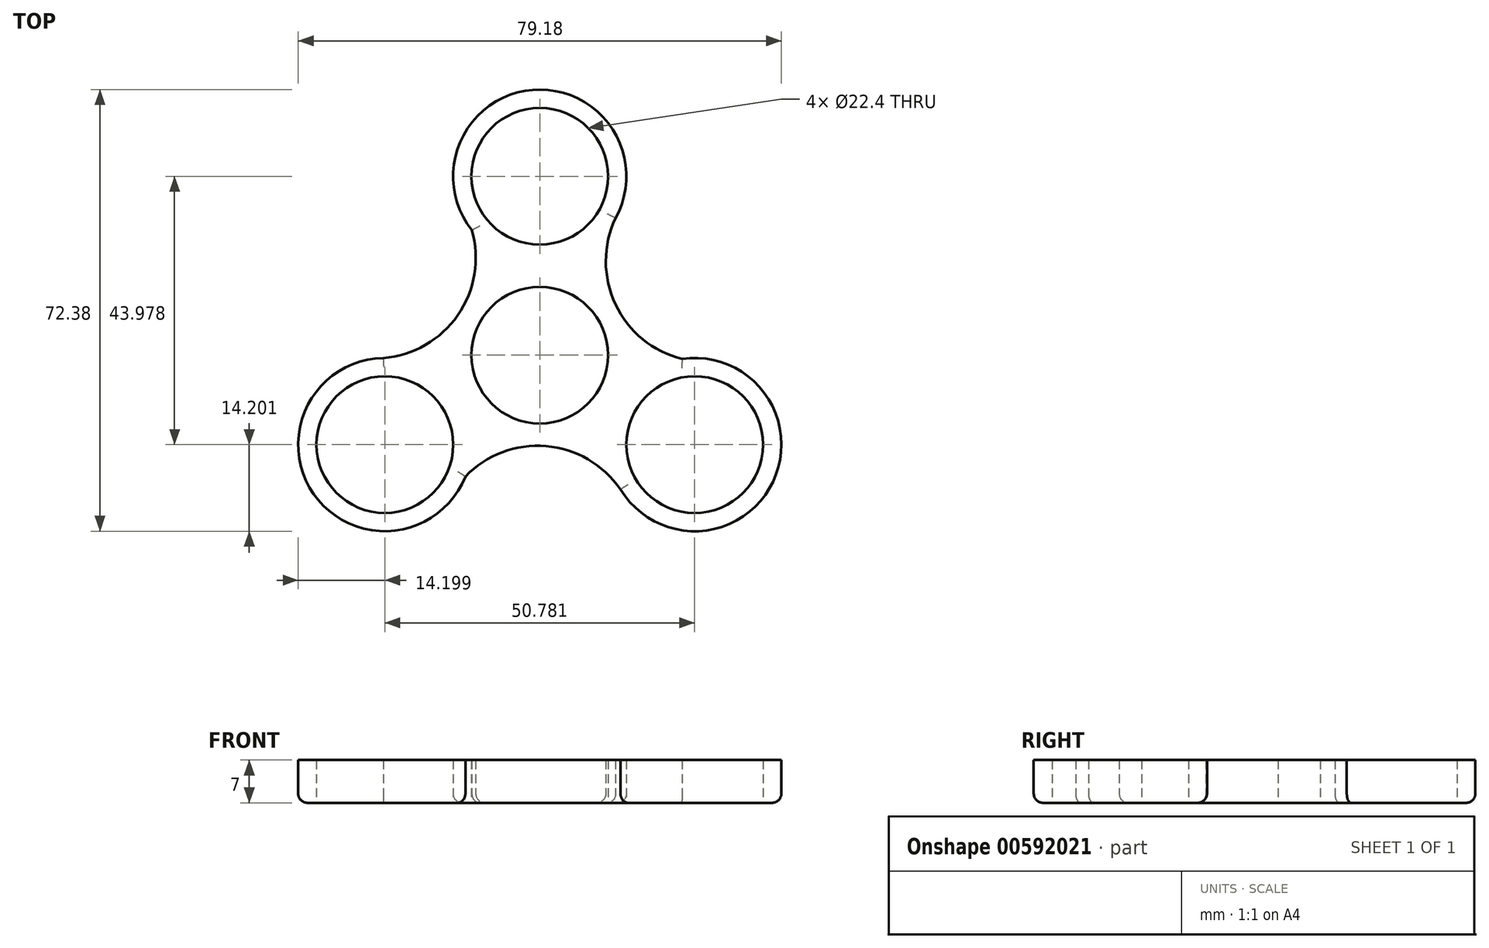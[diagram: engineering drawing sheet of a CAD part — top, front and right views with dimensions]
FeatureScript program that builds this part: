
annotation { "Feature Type Name" : "Feature", "Feature Type Description" : "" }
export const myFeature = defineFeature(function(context is Context, id is Id, definition is map)
    precondition{}
    {
        {
            var Q0;
            Q0=qCreatedBy(makeId("Top.planeOp"),FACE);
            var sketch = newSketch(context, id + "F0", { "sketchPlane" : qUnion([Q0])});
            skCircle(sketch, "E0", {"center": v(0, 0) * mm, "radius": 11.2 * mm});
            skCircle(sketch, "E1", {"center": v(0, 0) * mm, "radius": 14.2 * mm});
            skCircle(sketch, "E2", {"center": v(0, 29.32) * mm, "radius": 11.2 * mm});
            skCircle(sketch, "E3", {"center": v(0, 29.32) * mm, "radius": 14.2 * mm});
            skCircle(sketch, "E4.1.0", {"center": v(-25.4, -14.66) * mm, "radius": 11.2 * mm});
            skCircle(sketch, "E4.1.1", {"center": v(-25.4, -14.66) * mm, "radius": 14.2 * mm});
            skCircle(sketch, "E4.2.0", {"center": v(25.4, -14.66) * mm, "radius": 11.2 * mm});
            skCircle(sketch, "E4.2.1", {"center": v(25.4, -14.66) * mm, "radius": 14.2 * mm});
            skArc(sketch, "E5", {"start": v(12.43, 22.45) * mm, "mid": v(12.4, 8.34) * mm, "end": v(23.32, -0.61) * mm});
            skArc(sketch, "E6.1.0", {"start": v(-25.66, -0.46) * mm, "mid": v(-13.42, 6.57) * mm, "end": v(-11.13, 20.5) * mm});
            skArc(sketch, "E6.2.0", {"start": v(13.23, -21.99) * mm, "mid": v(1.02, -14.9) * mm, "end": v(-12.19, -19.9) * mm});
            skSolve(sketch);
        }
        {
            var Q0;
            Q0=makeQuery(id+"F0.imprint","IMPRINT",FACE,{"disambiguationData":[TD([[makeQuery(id+"F0.imprint","IMPRINT",EDGE,{"derivedFrom":sQuery(id+"F0.wireOp",EDGE,"E1")}),-1.0]])]});
            var Q1;
            Q1=makeQuery(id+"F0.imprint","IMPRINT",FACE,{"disambiguationData":[TD([[makeQuery(id+"F0.imprint","IMPRINT",EDGE,{"derivedFrom":sQuery(id+"F0.wireOp",EDGE,"E4.2.0")}),-1.0]])]});
            var Q2;
            Q2=makeQuery(id+"F0.imprint","IMPRINT",FACE,{"disambiguationData":[TD([[makeQuery(id+"F0.imprint","IMPRINT",EDGE,{"derivedFrom":sQuery(id+"F0.wireOp",EDGE,"E4.1.0")}),-1.0]])]});
            var Q3;
            Q3=makeQuery(id+"F0.imprint","IMPRINT",FACE,{"disambiguationData":[TD([[makeQuery(id+"F0.imprint","IMPRINT",EDGE,{"derivedFrom":sQuery(id+"F0.wireOp",EDGE,"E2")}),-1.0]])]});
            var Q4;
            Q4=makeQuery(id+"F0.imprint","IMPRINT",FACE,{"disambiguationData":[TD([[makeQuery(id+"F0.imprint","IMPRINT",EDGE,{"derivedFrom":sQuery(id+"F0.wireOp",EDGE,"E0")}),-1.0]])]});
            extrude(context, id + "F1", {"entities" : qUnion([Q0, Q1, Q2, Q3, Q4]), "depth" : 7 * mm, "offsetDistance" : 25 * mm});
        }
        {
            var Q0;
            Q0=makeQuery(id+"F1.opExtrude","CAP_EDGE",EDGE,{"disambiguationData":[OSD([sQuery(id+"F0.wireOp",EDGE,"E6.2.0")])],"isStart":true});
            var Q1;
            Q1=makeQuery(id+"F1.opExtrude","CAP_EDGE",EDGE,{"disambiguationData":[OSD([sQuery(id+"F0.wireOp",EDGE,"E4.2.1")])],"isStart":true});
            var Q2;
            Q2=makeQuery(id+"F1.opExtrude","CAP_EDGE",EDGE,{"disambiguationData":[OSD([sQuery(id+"F0.wireOp",EDGE,"E5")])],"isStart":true});
            var Q3;
            Q3=makeQuery(id+"F1.opExtrude","CAP_EDGE",EDGE,{"disambiguationData":[OSD([sQuery(id+"F0.wireOp",EDGE,"E3")])],"isStart":true});
            var Q4;
            Q4=makeQuery(id+"F1.opExtrude","CAP_EDGE",EDGE,{"disambiguationData":[OSD([sQuery(id+"F0.wireOp",EDGE,"E6.1.0")])],"isStart":true});
            var Q5;
            Q5=makeQuery(id+"F1.opExtrude","CAP_EDGE",EDGE,{"disambiguationData":[OSD([sQuery(id+"F0.wireOp",EDGE,"E4.1.1")])],"isStart":true});
            fillet(context, id + "F2", {"entities" : qUnion([Q0, Q1, Q2, Q3, Q4, Q5]), "radius" : 1.5 * mm, "tangentPropagation" : true, "allowEdgeOverflow" : false});
        }
    });
